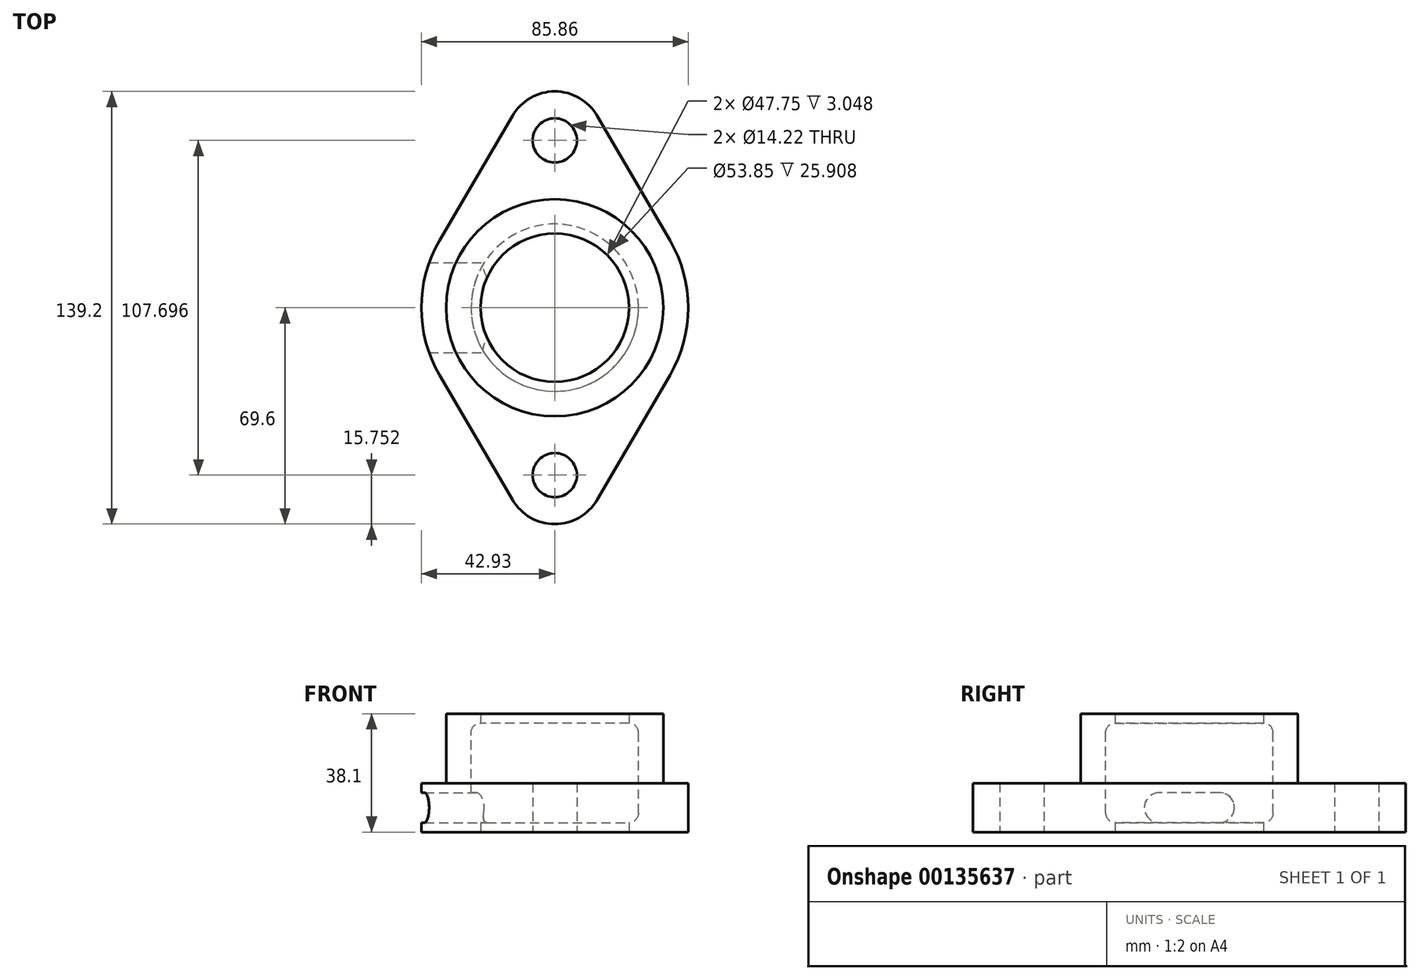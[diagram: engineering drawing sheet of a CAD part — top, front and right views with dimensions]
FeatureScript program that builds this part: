
annotation { "Feature Type Name" : "Feature", "Feature Type Description" : "" }
export const myFeature = defineFeature(function(context is Context, id is Id, definition is map)
    precondition{}
    {
        {
            var Q0;
            Q0=qCreatedBy(makeId("Top.planeOp"),FACE);
            var sketch = newSketch(context, id + "F0", { "sketchPlane" : qUnion([Q0])});
            skCircle(sketch, "E0", {"center": v(0, 0) * mm, "radius": 34.93 * mm});
            skCircle(sketch, "E1", {"center": v(0, 53.85) * mm, "radius": 7.11 * mm});
            skCircle(sketch, "E2", {"center": v(0, -53.85) * mm, "radius": 7.11 * mm});
            skLineSegment(sketch, "E3", {"start": v(-37.06, 21.67) * mm, "end": v(-13.6, 61.8) * mm});
            skArc(sketch, "E4", {"start": v(13.6, 61.8) * mm, "mid": v(0, 69.6) * mm, "end": v(-13.6, 61.8) * mm});
            skArc(sketch, "E5", {"start": v(-37.06, 21.67) * mm, "mid": v(-42.93, 0) * mm, "end": v(-37.06, -21.67) * mm});
            skLineSegment(sketch, "E6", {"start": v(-37.06, -21.67) * mm, "end": v(-13.6, -61.8) * mm});
            skArc(sketch, "E7", {"start": v(-13.6, -61.8) * mm, "mid": v(0, -69.6) * mm, "end": v(13.6, -61.8) * mm});
            skArc(sketch, "E8", {"start": v(37.06, -21.67) * mm, "mid": v(42.93, 0) * mm, "end": v(37.06, 21.67) * mm});
            skLineSegment(sketch, "E9", {"start": v(13.6, 61.8) * mm, "end": v(37.06, 21.67) * mm});
            skLineSegment(sketch, "E10", {"start": v(13.6, -61.8) * mm, "end": v(37.06, -21.67) * mm});
            skCircle(sketch, "E11", {"center": v(0, 0) * mm, "radius": 23.88 * mm});
            skSolve(sketch);
        }
        {
            var Q0;
            Q0 = qSketchRegion(id + "F0", true);
            extrude(context, id + "F1", {"entities" : qUnion([Q0]), "depth" : 15.75 * mm});
        }
        {
            var Q0;
            Q0=makeQuery(id+"F0.imprint","IMPRINT",FACE,{"disambiguationData":[TD([[makeQuery(id+"F0.imprint","IMPRINT",EDGE,{"derivedFrom":sQuery(id+"F0.wireOp",EDGE,"E0")}),1.0]])]});
            extrude(context, id + "F2", {"entities" : qUnion([Q0]), "operationType" : NewBodyOperationType.ADD, "depth" : 38.1 * mm});
        }
        {
            var Q0;
            Q0=qCreatedBy(makeId("Right.planeOp"),FACE);
            var sketch = newSketch(context, id + "F3", { "sketchPlane" : qUnion([Q0])});
            skLineSegment(sketch, "E12.bottom", {"start": v(0, 3.05) * mm, "end": v(23.88, 3.05) * mm});
            skLineSegment(sketch, "E12.top", {"start": v(0, 35.05) * mm, "end": v(23.88, 35.05) * mm});
            skLineSegment(sketch, "E12.left", {"start": v(0, 3.05) * mm, "end": v(0, 35.05) * mm});
            skLineSegment(sketch, "E12.right", {"start": v(26.92, 6.1) * mm, "end": v(26.92, 32) * mm});
            skPoint(sketch, "E13.visualSharp", {"position": v(26.92, 35.05) * mm});
            skArc(sketch, "E13.filletArc", {"start": v(26.92, 32) * mm, "mid": v(26.03, 34.16) * mm, "end": v(23.88, 35.05) * mm});
            skPoint(sketch, "E14.visualSharp", {"position": v(26.92, 3.05) * mm});
            skArc(sketch, "E14.filletArc", {"start": v(23.88, 3.05) * mm, "mid": v(26.03, 3.94) * mm, "end": v(26.92, 6.1) * mm});
            skSolve(sketch);
        }
        {
            var Q0;
            Q0 = qSketchRegion(id + "F3", true);
            var Q1;
            Q1=sQuery(id+"F3.wireOp",EDGE,"E12.left");
            revolve(context, id + "F4", {"operationType" : NewBodyOperationType.REMOVE, "entities" : qUnion([Q0]), "axis" : qUnion([Q1]), "revolveType" : RevolveType.FULL, "oppositeDirection" : true});
        }
        {
            var Q0;
            Q0=qCreatedBy(makeId("Right.planeOp"),FACE);
            var sketch = newSketch(context, id + "F5", { "sketchPlane" : qUnion([Q0])});
            skLineSegment(sketch, "E15.bottom", {"start": v(-9.65, 3.05) * mm, "end": v(9.65, 3.05) * mm});
            skArc(sketch, "E16", {"start": v(9.65, 3.05) * mm, "mid": v(14.48, 7.87) * mm, "end": v(9.65, 12.7) * mm});
            skLineSegment(sketch, "E17", {"start": v(9.65, 12.7) * mm, "end": v(-9.65, 12.7) * mm});
            skArc(sketch, "E18", {"start": v(-9.65, 12.7) * mm, "mid": v(-14.48, 7.87) * mm, "end": v(-9.65, 3.05) * mm});
            skSolve(sketch);
        }
        {
            var Q0;
            Q0 = qSketchRegion(id + "F5", true);
            extrude(context, id + "F6", {"entities" : qUnion([Q0]), "operationType" : NewBodyOperationType.REMOVE, "endBound" : BoundingType.THROUGH_ALL, "oppositeDirection" : true, "depth" : 25.4 * mm});
        }
    });
